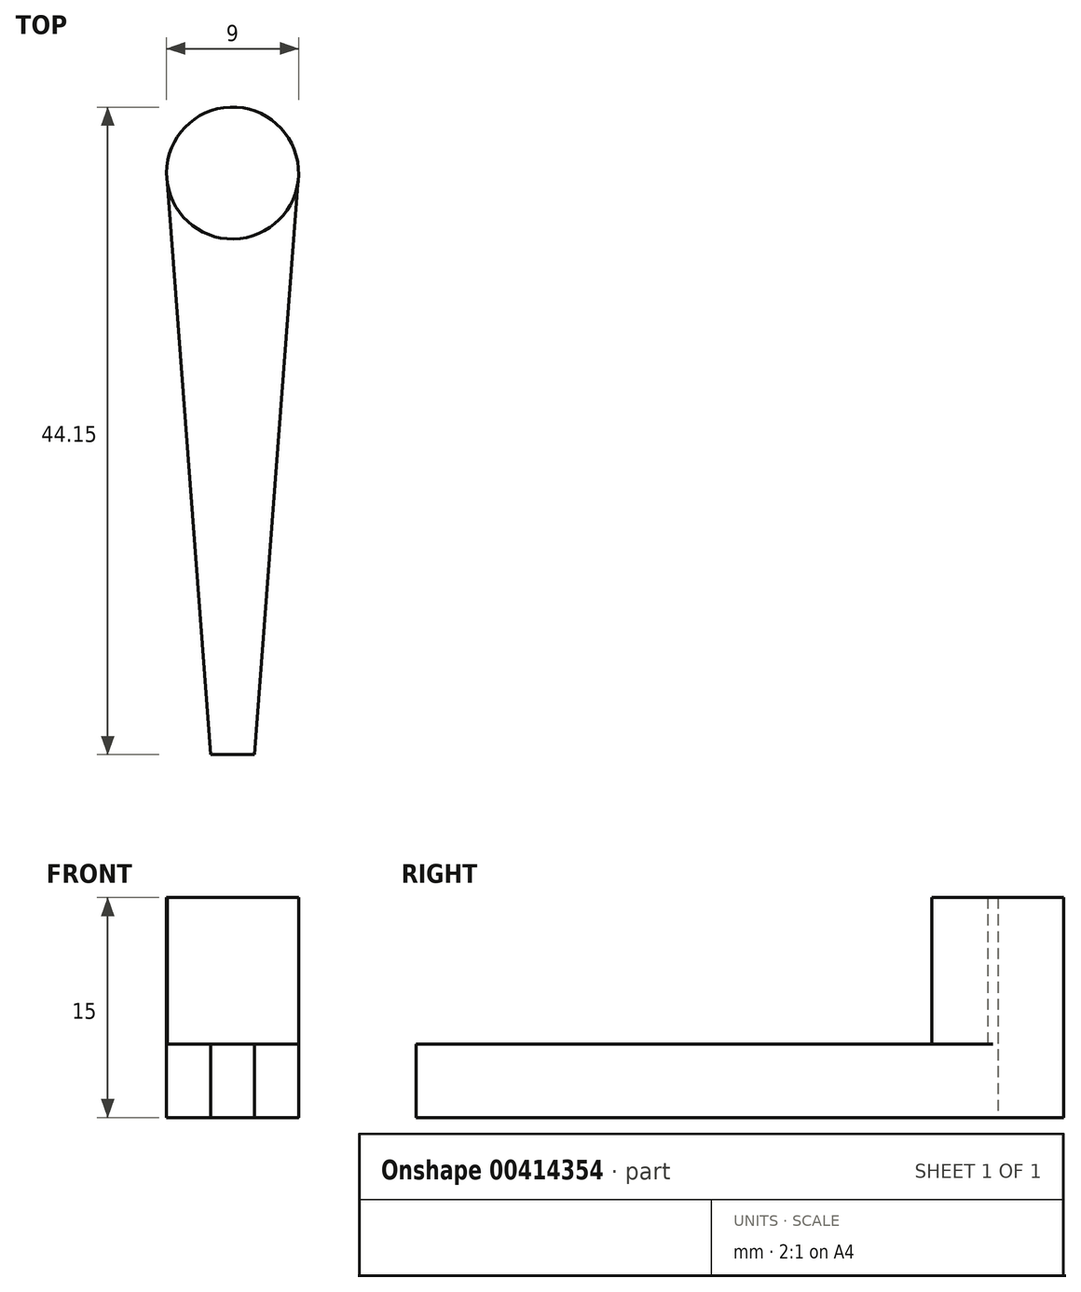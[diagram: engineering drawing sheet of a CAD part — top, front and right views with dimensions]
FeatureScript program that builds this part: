
annotation { "Feature Type Name" : "Feature", "Feature Type Description" : "" }
export const myFeature = defineFeature(function(context is Context, id is Id, definition is map)
    precondition{}
    {
        {
            var Q0;
            Q0=qCreatedBy(makeId("Top.planeOp"),FACE);
            var sketch = newSketch(context, id + "F0", { "sketchPlane" : qUnion([Q0])});
            skCircle(sketch, "E0", {"center": v(0, 0) * mm, "radius": 4.5 * mm});
            skLineSegment(sketch, "E1", {"start": v(-4.5, 0) * mm, "end": v(-1.5, -39.65) * mm});
            skLineSegment(sketch, "E2", {"start": v(1.5, -39.65) * mm, "end": v(4.51, 0) * mm});
            skLineSegment(sketch, "E3", {"start": v(-1.5, -39.65) * mm, "end": v(1.5, -39.65) * mm});
            skSolve(sketch);
        }
        {
            var Q0;
            {var subQ5=sQuery(id+"F0.wireOp",EDGE,"E3");Q0=makeQuery(id+"F0.imprint","IMPRINT",FACE,{"disambiguationData":[TD([[makeQuery(id+"F0.imprint","IMPRINT",EDGE,{"derivedFrom":subQ5}),1.0]])]});}
            extrude(context, id + "F1", {"entities" : qUnion([Q0]), "depth" : 5 * mm});
        }
        {
            var Q0;
            {var subQ0=sQuery(id+"F0.wireOp",EDGE,"E0");var subQ1=makeQuery(id+"F0.imprint","INTERSECT",VERTEX,{"derivedFrom":[subQ0,sQuery(id+"F0.wireOp",EDGE,"E2")]});Q0=makeQuery(id+"F0.imprint","IMPRINT",FACE,{"disambiguationData":[TD([[makeQuery(id+"F0.imprint","IMPRINT",EDGE,{"disambiguationData":[TD([[subQ1,1.0]])],"derivedFrom":subQ0}),1.0]])]});}
            extrude(context, id + "F2", {"entities" : qUnion([Q0]), "operationType" : NewBodyOperationType.ADD, "depth" : 15 * mm});
        }
    });
